# Revit family: 3-806-XX PALILLO PENDANT
name_source: partatom
category: Lighting Fixtures
units: mm (PartAtom-declared; Revit-internal decimal feet)

## family parameters
Always vertical = Yes
Cut with Voids When Loaded = No
Host = Ceiling
Light Source = Yes
OmniClass Number = 23.80.70.11
OmniClass Title = Luminaries for Internal Lighting
Part Type = Normal
Room Calculation Point = No
Round Connector Dimension = Use Diameter
Shared = No

## types (2) — shared parameters
Color Filter = 16777215
Diffusers = Matte White Acrylic
Dimming Lamp Color Temperature Shift = <None>
Lamp = LED Array
Light Source Symbol Size = 24"
Manufacturer = Oxygen Lighting and Fans
Model = 3-804-xx / Palillo Pendant
References = Ref. 3 = 120 V / Ref. 37 = 277 V
URL = www.oxygenlighting.com
Voltage = 120 V
Voltage Input = 120 V or 277 V - 50/60 Hz
Wattage Comments = 6 x 8.5 W at 120 V

## per-type parameters (varying)
| type | Metal Finish | Pendant height |
| 3-806-15 / Black - Matte White Acrylic | 15 - Black | 26" |
| 3-806-40 / Aged Brass - Matte White Acrylic | 40 - Aged Brass | 23" |

## geometry (parser evidence)
native form markers: Extrusion x1, Sweep x6
no freeform markers — native parametric forms only
